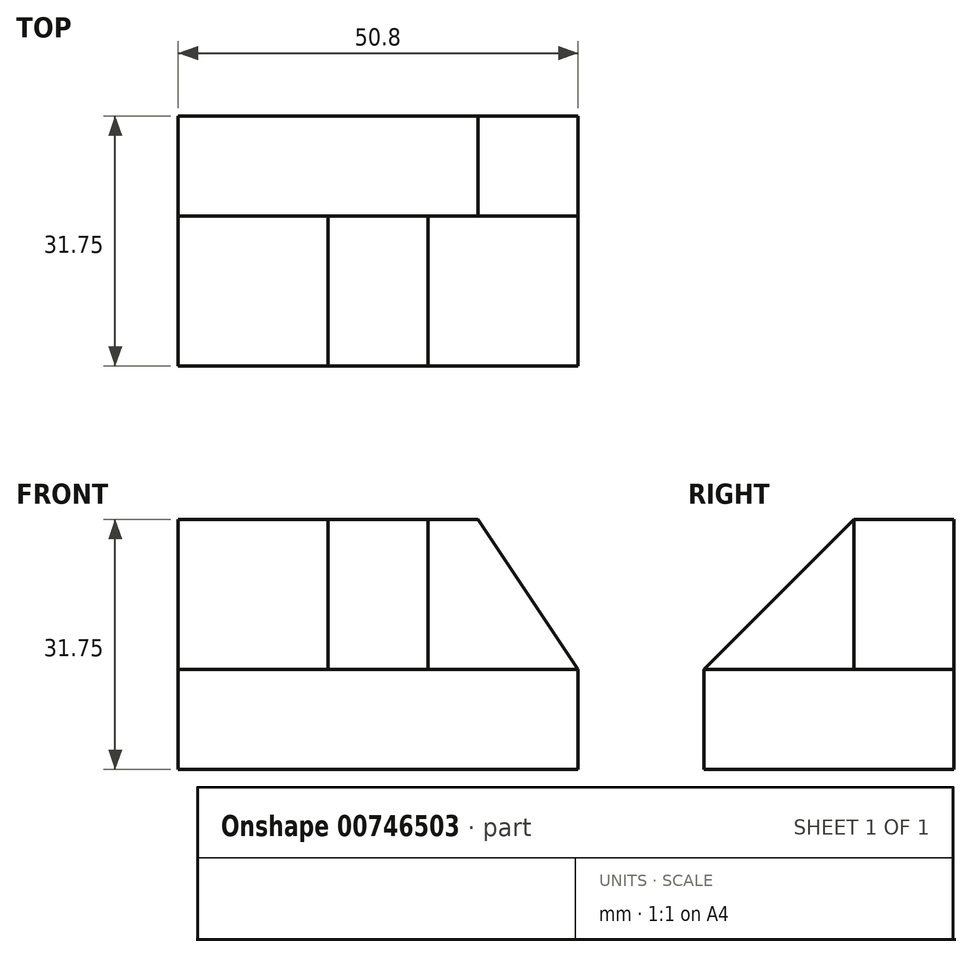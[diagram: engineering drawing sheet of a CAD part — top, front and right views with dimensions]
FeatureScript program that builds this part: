
annotation { "Feature Type Name" : "Feature", "Feature Type Description" : "" }
export const myFeature = defineFeature(function(context is Context, id is Id, definition is map)
    precondition{}
    {
        {
            var Q0;
            Q0=qCreatedBy(makeId("Front.planeOp"),FACE);
            var sketch = newSketch(context, id + "F0", { "sketchPlane" : qUnion([Q0])});
            skLineSegment(sketch, "E0", {"start": v(0, 0) * mm, "end": v(50.8, 0) * mm});
            skLineSegment(sketch, "E1", {"start": v(50.8, 0) * mm, "end": v(50.8, 31.75) * mm});
            skLineSegment(sketch, "E2", {"start": v(50.8, 31.75) * mm, "end": v(0, 31.75) * mm});
            skLineSegment(sketch, "E3", {"start": v(0, 31.75) * mm, "end": v(0, 0) * mm});
            skSolve(sketch);
        }
        {
            var Q0;
            Q0=makeQuery(id+"F0.imprint","IMPRINT",FACE,{"disambiguationData":[TD([[makeQuery(id+"F0.imprint","IMPRINT",EDGE,{"derivedFrom":sQuery(id+"F0.wireOp",EDGE,"E0")}),1.0]])]});
            var Q1;
            Q1 = qSketchRegion(id + "FDDblSgq03aiGt0_1", true);
            extrude(context, id + "F1", {"entities" : qUnion([Q0, Q1]), "depth" : 31.75 * mm, "offsetDistance" : 25.4 * mm});
        }
        {
            var Q0;
            Q0=makeQuery(id+"F1.opExtrude","CAP_FACE",FACE,{"disambiguationData":[OSD([sQuery(id+"F0.wireOp",EDGE,"E0"),sQuery(id+"F0.wireOp",EDGE,"E1"),sQuery(id+"F0.wireOp",EDGE,"E2"),sQuery(id+"F0.wireOp",EDGE,"E3")])],"isStart":false});
            var sketch = newSketch(context, id + "F2", { "sketchPlane" : qUnion([Q0])});
            skLineSegment(sketch, "E4", {"start": v(31.75, 31.75) * mm, "end": v(31.75, 12.7) * mm});
            skLineSegment(sketch, "E5", {"start": v(31.75, 12.7) * mm, "end": v(50.8, 12.7) * mm});
            skLineSegment(sketch, "E6", {"start": v(50.8, 12.7) * mm, "end": v(50.8, 31.75) * mm});
            skLineSegment(sketch, "E7", {"start": v(50.8, 31.75) * mm, "end": v(31.75, 31.75) * mm});
            skSolve(sketch);
        }
        {
            var Q0;
            Q0=makeQuery(id+"F2.imprint","IMPRINT",FACE,{"disambiguationData":[TD([[makeQuery(id+"F2.imprint","IMPRINT",EDGE,{"derivedFrom":sQuery(id+"F2.wireOp",EDGE,"E4")}),1.0]])]});
            extrude(context, id + "F3", {"entities" : qUnion([Q0]), "operationType" : NewBodyOperationType.REMOVE, "oppositeDirection" : true, "depth" : 19.05 * mm, "offsetDistance" : 25.4 * mm});
        }
        {
            var Q0;
            Q0=makeQuery(id+"F1.opExtrude","CAP_FACE",FACE,{"disambiguationData":[OSD([sQuery(id+"F0.wireOp",EDGE,"E0"),sQuery(id+"F0.wireOp",EDGE,"E1"),sQuery(id+"F0.wireOp",EDGE,"E2"),sQuery(id+"F0.wireOp",EDGE,"E3")])],"isStart":false});
            var sketch = newSketch(context, id + "F4", { "sketchPlane" : qUnion([Q0])});
            skLineSegment(sketch, "E8", {"start": v(19.05, 31.75) * mm, "end": v(19.05, 12.7) * mm});
            skLineSegment(sketch, "E9", {"start": v(19.05, 12.7) * mm, "end": v(0, 12.7) * mm});
            skLineSegment(sketch, "E10", {"start": v(0, 12.7) * mm, "end": v(0, 31.75) * mm});
            skLineSegment(sketch, "E11", {"start": v(0, 31.75) * mm, "end": v(19.05, 31.75) * mm});
            skSolve(sketch);
        }
        {
            var Q0;
            Q0=makeQuery(id+"F4.imprint","IMPRINT",FACE,{"disambiguationData":[TD([[makeQuery(id+"F4.imprint","IMPRINT",EDGE,{"derivedFrom":sQuery(id+"F4.wireOp",EDGE,"E8")}),-1.0]])]});
            extrude(context, id + "F5", {"entities" : qUnion([Q0]), "operationType" : NewBodyOperationType.REMOVE, "oppositeDirection" : true, "depth" : 19.05 * mm, "offsetDistance" : 25.4 * mm});
        }
        {
            var Q0;
            Q0=makeQuery(id+"F3.boolean.opBoolean","COPY",FACE,{"derivedFrom":makeQuery(id+"F3.opExtrude","SWEPT_FACE",FACE,{"disambiguationData":[OSD([sQuery(id+"F2.wireOp",EDGE,"E4")])]})});
            var sketch = newSketch(context, id + "F6", { "sketchPlane" : qUnion([Q0])});
            skLineSegment(sketch, "E12", {"start": v(-31.75, 12.7) * mm, "end": v(-12.7, 31.75) * mm});
            skLineSegment(sketch, "E13", {"start": v(-12.7, 31.75) * mm, "end": v(-31.75, 31.75) * mm});
            skLineSegment(sketch, "E14", {"start": v(-31.75, 31.75) * mm, "end": v(-31.75, 12.7) * mm});
            skSolve(sketch);
        }
        {
            var Q0;
            Q0=makeQuery(id+"F6.imprint","IMPRINT",FACE,{"disambiguationData":[TD([[makeQuery(id+"F6.imprint","IMPRINT",EDGE,{"derivedFrom":sQuery(id+"F6.wireOp",EDGE,"E12")}),1.0]])]});
            extrude(context, id + "F7", {"entities" : qUnion([Q0]), "operationType" : NewBodyOperationType.REMOVE, "oppositeDirection" : true, "depth" : 25.4 * mm, "offsetDistance" : 25.4 * mm});
        }
        {
            var Q0;
            Q0=makeQuery(id+"F3.boolean.opBoolean","COPY",FACE,{"derivedFrom":makeQuery(id+"F3.opExtrude","CAP_FACE",FACE,{"disambiguationData":[OSD([sQuery(id+"F2.wireOp",EDGE,"E4"),sQuery(id+"F2.wireOp",EDGE,"E5"),sQuery(id+"F2.wireOp",EDGE,"E6"),sQuery(id+"F2.wireOp",EDGE,"E7")])],"isStart":false})});
            var sketch = newSketch(context, id + "F8", { "sketchPlane" : qUnion([Q0])});
            skLineSegment(sketch, "E15", {"start": v(38.1, 31.75) * mm, "end": v(50.8, 12.7) * mm});
            skLineSegment(sketch, "E16", {"start": v(50.8, 12.7) * mm, "end": v(50.8, 31.75) * mm});
            skLineSegment(sketch, "E17", {"start": v(50.8, 31.75) * mm, "end": v(38.1, 31.75) * mm});
            skSolve(sketch);
        }
        {
            var Q0;
            Q0=makeQuery(id+"F8.imprint","IMPRINT",FACE,{"disambiguationData":[TD([[makeQuery(id+"F8.imprint","IMPRINT",EDGE,{"derivedFrom":sQuery(id+"F8.wireOp",EDGE,"E15")}),1.0]])]});
            extrude(context, id + "F9", {"entities" : qUnion([Q0]), "operationType" : NewBodyOperationType.REMOVE, "oppositeDirection" : true, "depth" : 25.4 * mm, "offsetDistance" : 25.4 * mm});
        }
    });
